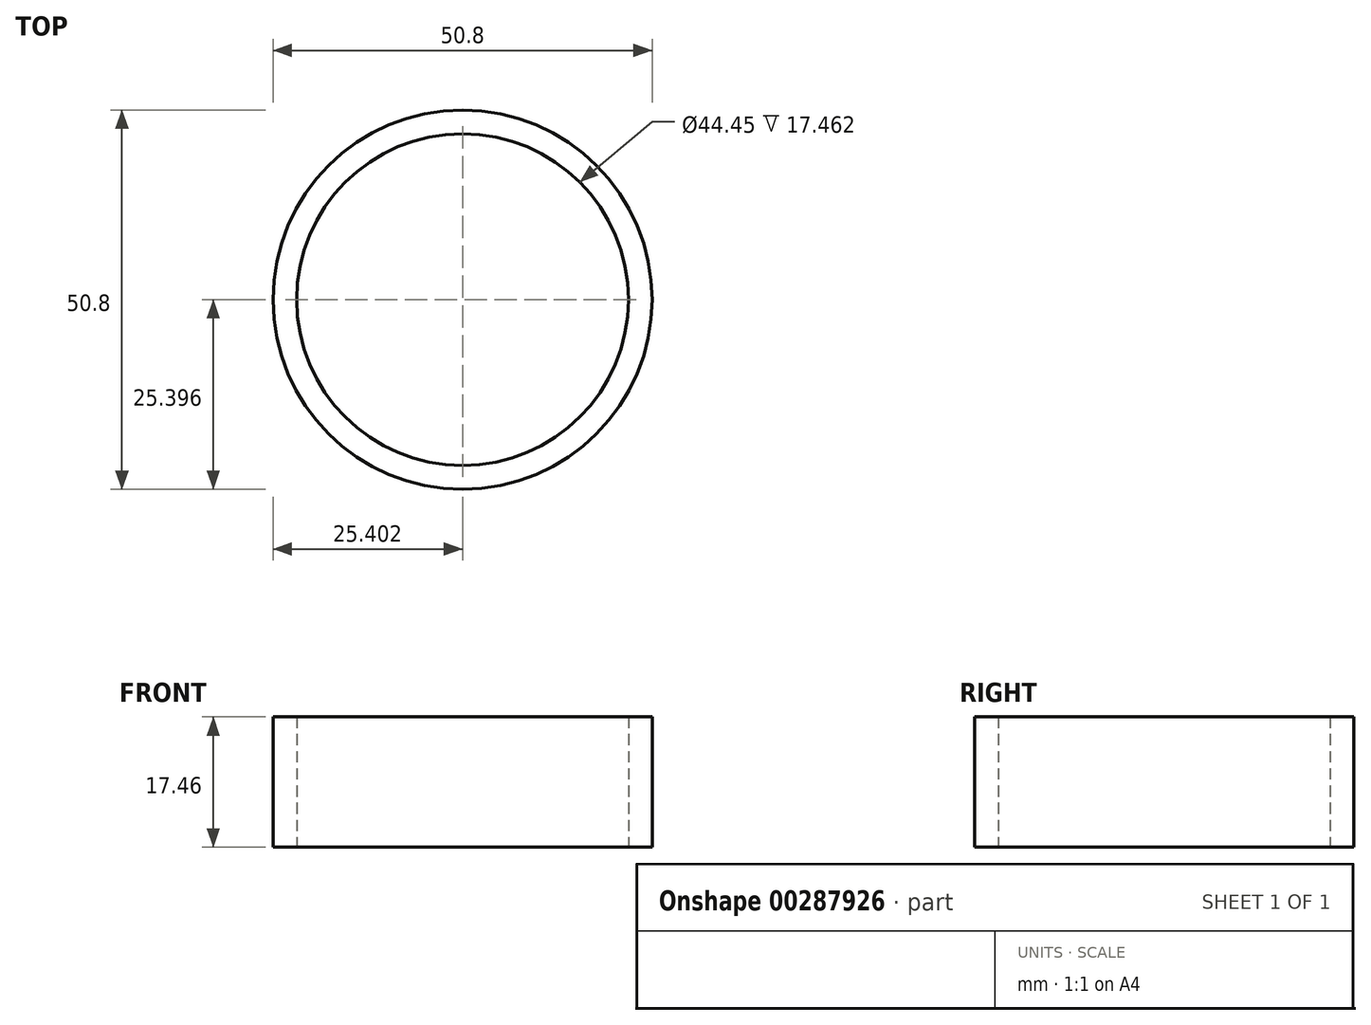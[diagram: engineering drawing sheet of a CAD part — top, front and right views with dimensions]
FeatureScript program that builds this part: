
annotation { "Feature Type Name" : "Feature", "Feature Type Description" : "" }
export const myFeature = defineFeature(function(context is Context, id is Id, definition is map)
    precondition{}
    {
        {
            var Q0;
            Q0=qCreatedBy(makeId("Top.planeOp"),FACE);
            var sketch = newSketch(context, id + "F0", { "sketchPlane" : qUnion([Q0])});
            skCircle(sketch, "E0", {"center": v(-40.5, 26.5) * mm, "radius": 22.23 * mm});
            skCircle(sketch, "E1", {"center": v(-40.5, 26.5) * mm, "radius": 25.4 * mm});
            skSolve(sketch);
        }
        {
            var Q0;
            Q0=makeQuery(id+"F0.imprint","IMPRINT",FACE,{"disambiguationData":[TD([[makeQuery(id+"F0.imprint","IMPRINT",EDGE,{"derivedFrom":sQuery(id+"F0.wireOp",EDGE,"E0")}),-1.0]])]});
            extrude(context, id + "F1", {"entities" : qUnion([Q0]), "depth" : 17.46 * mm, "offsetDistance" : 25.4 * mm});
        }
    });
